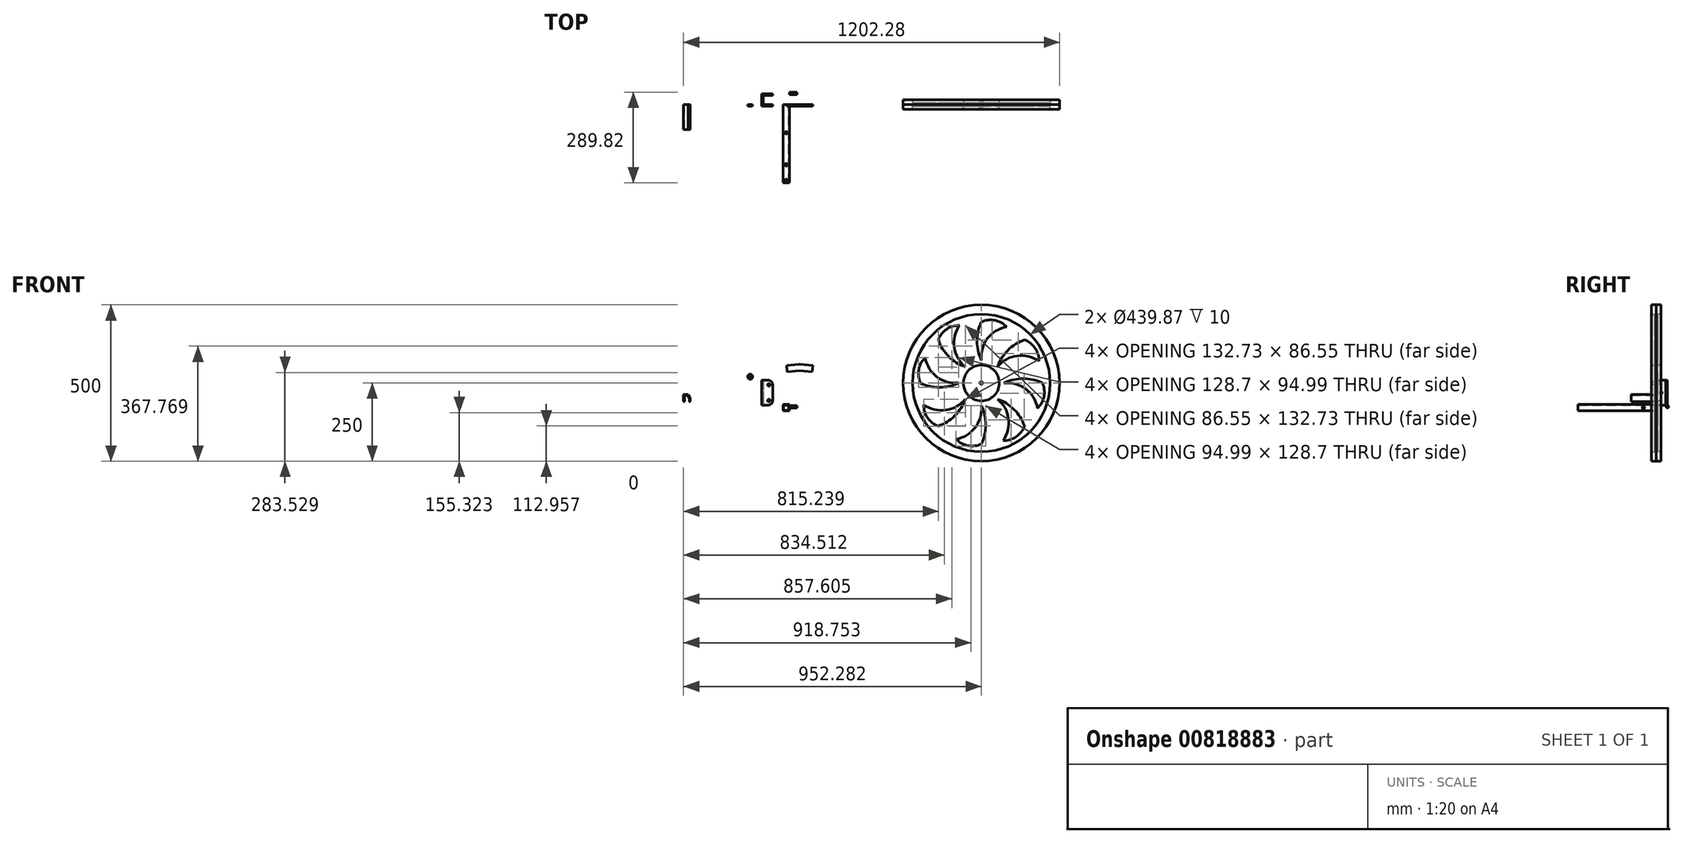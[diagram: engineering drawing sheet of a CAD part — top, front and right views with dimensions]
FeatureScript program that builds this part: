
annotation { "Feature Type Name" : "Feature", "Feature Type Description" : "" }
export const myFeature = defineFeature(function(context is Context, id is Id, definition is map)
    precondition{}
    {
        {
            var Q0;
            Q0=qCreatedBy(makeId("Front.planeOp"),FACE);
            var sketch = newSketch(context, id + "F0", { "sketchPlane" : qUnion([Q0])});
            skLineSegment(sketch, "E0.bottom", {"start": v(15, 40) * mm, "end": v(-15, 40) * mm});
            skLineSegment(sketch, "E0.top", {"start": v(15, -40) * mm, "end": v(-15, -40) * mm});
            skLineSegment(sketch, "E0.left", {"start": v(15, 40) * mm, "end": v(15, -40) * mm});
            skLineSegment(sketch, "E0.right", {"start": v(-15, 40) * mm, "end": v(-15, -40) * mm});
            skPoint(sketch, "E0.middle", {"position": v(0, 0) * mm});
            skLineSegment(sketch, "E1.bottom", {"start": v(-15, -40) * mm, "end": v(-20, -40) * mm});
            skLineSegment(sketch, "E1.top", {"start": v(-15, 40) * mm, "end": v(-20, 40) * mm});
            skLineSegment(sketch, "E1.left", {"start": v(-15, -40) * mm, "end": v(-15, 40) * mm});
            skLineSegment(sketch, "E1.right", {"start": v(-20, -40) * mm, "end": v(-20, 40) * mm});
            skCircle(sketch, "E2", {"center": v(3, 25) * mm, "radius": 4 * mm});
            skLineSegment(sketch, "E3", {"start": v(-15, 0) * mm, "end": v(9.6, 0) * mm, "construction": true});
            skCircle(sketch, "E4.MirrorC", {"center": v(3, -25) * mm, "radius": 4 * mm});
            skLineSegment(sketch, "E5.bottom", {"start": v(68.16, -57.9) * mm, "end": v(48.16, -57.9) * mm});
            skLineSegment(sketch, "E5.top", {"start": v(68.16, -37.9) * mm, "end": v(48.16, -37.9) * mm});
            skLineSegment(sketch, "E5.left", {"start": v(68.16, -57.9) * mm, "end": v(68.16, -37.9) * mm});
            skLineSegment(sketch, "E5.right", {"start": v(48.16, -57.9) * mm, "end": v(48.16, -37.9) * mm});
            skLineSegment(sketch, "E6.0", {"start": v(66.66, -56.4) * mm, "end": v(49.66, -56.4) * mm});
            skLineSegment(sketch, "E6.1", {"start": v(66.66, -56.4) * mm, "end": v(66.66, -39.4) * mm});
            skLineSegment(sketch, "E6.2", {"start": v(66.66, -39.4) * mm, "end": v(49.66, -39.4) * mm});
            skLineSegment(sketch, "E6.3", {"start": v(49.66, -56.4) * mm, "end": v(49.66, -39.4) * mm});
            skCircle(sketch, "E7", {"center": v(682.3, 30.98) * mm, "radius": 250 * mm});
            skCircle(sketch, "E8", {"center": v(682.3, 30.98) * mm, "radius": 57.27 * mm});
            skCircle(sketch, "E9", {"center": v(682.3, 30.98) * mm, "radius": 219.94 * mm});
            skCircle(sketch, "E10", {"center": v(682.3, 30.98) * mm, "radius": 4 * mm});
            skLineSegment(sketch, "E11", {"start": v(61.67, 67.05) * mm, "end": v(101.52, 70.54) * mm});
            skLineSegment(sketch, "E12", {"start": v(61.67, 67.05) * mm, "end": v(59.93, 86.98) * mm});
            skLineSegment(sketch, "E13", {"start": v(59.93, 86.98) * mm, "end": v(99.77, 90.46) * mm});
            skLineSegment(sketch, "E14", {"start": v(101.52, 70.54) * mm, "end": v(99.77, 90.46) * mm, "construction": true});
            skLineSegment(sketch, "E15", {"start": v(101.52, 70.54) * mm, "end": v(101.52, 109.2) * mm, "construction": true});
            skLineSegment(sketch, "E16.MirrorCS", {"start": v(101.52, 70.54) * mm, "end": v(103.26, 90.46) * mm, "construction": true});
            skLineSegment(sketch, "E17.MirrorCS", {"start": v(143.1, 86.98) * mm, "end": v(103.26, 90.46) * mm});
            skLineSegment(sketch, "E18.MirrorCS", {"start": v(141.36, 67.05) * mm, "end": v(143.1, 86.98) * mm});
            skLineSegment(sketch, "E19.MirrorCS", {"start": v(141.36, 67.05) * mm, "end": v(101.52, 70.54) * mm});
            skLineSegment(sketch, "E20", {"start": v(99.77, 90.46) * mm, "end": v(103.26, 90.46) * mm});
            skCircle(sketch, "E21", {"center": v(-56.88, 51) * mm, "radius": 8 * mm});
            skCircle(sketch, "E22", {"center": v(-56.88, 51) * mm, "radius": 4 * mm});
            skLineSegment(sketch, "E23.bottom", {"start": v(-266.99, -8.83) * mm, "end": v(-256.99, -8.83) * mm});
            skLineSegment(sketch, "E23.top", {"start": v(-266.99, -28.83) * mm, "end": v(-256.99, -28.83) * mm});
            skLineSegment(sketch, "E23.left", {"start": v(-266.99, -8.83) * mm, "end": v(-266.99, -28.83) * mm});
            skLineSegment(sketch, "E23.right", {"start": v(-256.99, -8.83) * mm, "end": v(-256.99, -28.83) * mm});
            skLineSegment(sketch, "E24", {"start": v(-256.99, -8.83) * mm, "end": v(-251.45, -18.83) * mm});
            skPoint(sketch, "E24.endSnap0", {"position": v(-256.99, -18.83) * mm});
            skLineSegment(sketch, "E25.0", {"start": v(-269.99, -5.83) * mm, "end": v(-269.99, -28.83) * mm});
            skLineSegment(sketch, "E25.1", {"start": v(-269.99, -5.83) * mm, "end": v(-255.22, -5.83) * mm});
            skLineSegment(sketch, "E25.2", {"start": v(-255.22, -5.83) * mm, "end": v(-248.83, -17.37) * mm});
            skLineSegment(sketch, "E26", {"start": v(-269.99, -28.83) * mm, "end": v(-266.99, -28.83) * mm});
            skLineSegment(sketch, "E27", {"start": v(-251.45, -18.83) * mm, "end": v(-251.45, -28.86) * mm});
            skLineSegment(sketch, "E28", {"start": v(-251.45, -28.86) * mm, "end": v(-248.83, -28.86) * mm});
            skLineSegment(sketch, "E29", {"start": v(-248.83, -28.86) * mm, "end": v(-248.83, -17.37) * mm});
            skArc(sketch, "E30", {"start": v(601.27, -148.4) * mm, "mid": v(662.98, -111.16) * mm, "end": v(682.3, -41.72) * mm});
            skArc(sketch, "E31", {"start": v(682.3, -164.11) * mm, "mid": v(696.26, -102.91) * mm, "end": v(682.3, -41.72) * mm});
            skArc(sketch, "E32", {"start": v(601.27, -148.4) * mm, "mid": v(639.28, -169.16) * mm, "end": v(682.3, -164.11) * mm});
            skArc(sketch, "E33.1.0", {"start": v(751.85, -153.16) * mm, "mid": v(769.15, -83.18) * mm, "end": v(733.7, -20.42) * mm});
            skArc(sketch, "E33.1.1", {"start": v(751.85, -153.16) * mm, "mid": v(793.4, -140.95) * mm, "end": v(820.24, -106.97) * mm});
            skArc(sketch, "E33.1.2", {"start": v(820.24, -106.97) * mm, "mid": v(786.84, -53.82) * mm, "end": v(733.7, -20.42) * mm});
            skArc(sketch, "E33.2.0", {"start": v(861.68, -50.04) * mm, "mid": v(824.43, 11.67) * mm, "end": v(754.99, 30.98) * mm});
            skArc(sketch, "E33.2.1", {"start": v(861.68, -50.04) * mm, "mid": v(882.43, -12.03) * mm, "end": v(877.38, 30.98) * mm});
            skArc(sketch, "E33.2.2", {"start": v(877.38, 30.98) * mm, "mid": v(816.18, 44.94) * mm, "end": v(754.99, 30.98) * mm});
            skArc(sketch, "E33.3.0", {"start": v(866.43, 100.53) * mm, "mid": v(796.45, 117.84) * mm, "end": v(733.7, 82.38) * mm});
            skArc(sketch, "E33.3.1", {"start": v(866.43, 100.53) * mm, "mid": v(854.22, 142.08) * mm, "end": v(820.24, 168.93) * mm});
            skArc(sketch, "E33.3.2", {"start": v(820.24, 168.93) * mm, "mid": v(767.1, 135.53) * mm, "end": v(733.7, 82.38) * mm});
            skArc(sketch, "E33.4.0", {"start": v(763.31, 210.37) * mm, "mid": v(701.6, 173.12) * mm, "end": v(682.3, 103.67) * mm});
            skArc(sketch, "E33.4.1", {"start": v(763.31, 210.37) * mm, "mid": v(725.3, 231.12) * mm, "end": v(682.3, 226.07) * mm});
            skArc(sketch, "E33.4.2", {"start": v(682.3, 226.07) * mm, "mid": v(668.33, 164.87) * mm, "end": v(682.3, 103.67) * mm});
            skArc(sketch, "E33.5.0", {"start": v(612.74, 215.12) * mm, "mid": v(595.43, 145.14) * mm, "end": v(630.89, 82.38) * mm});
            skArc(sketch, "E33.5.1", {"start": v(612.74, 215.12) * mm, "mid": v(571.19, 202.91) * mm, "end": v(544.34, 168.93) * mm});
            skArc(sketch, "E33.5.2", {"start": v(544.34, 168.93) * mm, "mid": v(577.74, 115.78) * mm, "end": v(630.89, 82.38) * mm});
            skArc(sketch, "E33.6.0", {"start": v(502.9, 112) * mm, "mid": v(540.15, 50.29) * mm, "end": v(609.6, 30.98) * mm});
            skArc(sketch, "E33.6.1", {"start": v(502.9, 112) * mm, "mid": v(482.15, 74) * mm, "end": v(487.2, 30.98) * mm});
            skArc(sketch, "E33.6.2", {"start": v(487.2, 30.98) * mm, "mid": v(548.4, 17.02) * mm, "end": v(609.6, 30.98) * mm});
            skArc(sketch, "E33.7.0", {"start": v(498.16, -38.57) * mm, "mid": v(568.13, -55.88) * mm, "end": v(630.89, -20.42) * mm});
            skArc(sketch, "E33.7.1", {"start": v(498.16, -38.57) * mm, "mid": v(510.36, -80.13) * mm, "end": v(544.34, -106.97) * mm});
            skArc(sketch, "E33.7.2", {"start": v(544.34, -106.97) * mm, "mid": v(597.49, -73.57) * mm, "end": v(630.89, -20.42) * mm});
            skSolve(sketch);
        }
        {
            var Q0;
            Q0=makeQuery(id+"F0.imprint","IMPRINT",FACE,{"disambiguationData":[TD([[makeQuery(id+"F0.imprint","IMPRINT",EDGE,{"derivedFrom":sQuery(id+"F0.wireOp",EDGE,"E1.bottom")}),-1.0]])]});
            var Q1;
            Q1=makeQuery(id+"F0.imprint","IMPRINT",FACE,{"disambiguationData":[TD([[makeQuery(id+"F0.imprint","IMPRINT",EDGE,{"derivedFrom":sQuery(id+"F0.wireOp",EDGE,"E0.bottom")}),1.0]])]});
            extrude(context, id + "F1", {"entities" : qUnion([Q0, Q1]), "depth" : 5 * mm, "offsetDistance" : 25 * mm});
        }
        {
            var Q0;
            Q0=makeQuery(id+"F0.imprint","IMPRINT",FACE,{"disambiguationData":[TD([[makeQuery(id+"F0.imprint","IMPRINT",EDGE,{"derivedFrom":sQuery(id+"F0.wireOp",EDGE,"E1.bottom")}),-1.0]])]});
            extrude(context, id + "F2", {"entities" : qUnion([Q0]), "operationType" : NewBodyOperationType.ADD, "oppositeDirection" : true, "depth" : 15 * mm, "offsetDistance" : 25 * mm});
        }
        {
            var Q0;
            Q0=makeQuery(id+"F1.opExtrude","SWEPT_BODY",BODY,{"disambiguationData":[OSD([sQuery(id+"F0.wireOp",EDGE,"E0.bottom"),sQuery(id+"F0.wireOp",EDGE,"E0.top"),sQuery(id+"F0.wireOp",EDGE,"E0.left"),sQuery(id+"F0.wireOp",EDGE,"E1.bottom"),sQuery(id+"F0.wireOp",EDGE,"E1.top"),sQuery(id+"F0.wireOp",EDGE,"E1.right"),sQuery(id+"F0.wireOp",EDGE,"E2"),sQuery(id+"F0.wireOp",EDGE,"E4.MirrorC")])]});
            var Q1;
            Q1=makeQuery(id+"F2.opExtrude","CAP_FACE",FACE,{"disambiguationData":[OSD([sQuery(id+"F0.wireOp",EDGE,"E1.bottom"),sQuery(id+"F0.wireOp",EDGE,"E1.top"),sQuery(id+"F0.wireOp",EDGE,"E1.left"),sQuery(id+"F0.wireOp",EDGE,"E1.right")])],"isStart":false});
            mirror(context, id + "F3", {"operationType" : NewBodyOperationType.ADD, "entities" : qUnion([Q0]), "mirrorPlane" : qUnion([Q1])});
        }
        {
            var Q0;
            {var subQ0=sQuery(id+"F0.wireOp",EDGE,"E1.right");var subQ1=makeQuery(id+"F2.boolean.opBoolean","MERGE",FACE,{"derivedFrom":[makeQuery(id+"F1.opExtrude","SWEPT_FACE",FACE,{"disambiguationData":[OSD([subQ0])]}),makeQuery(id+"F2.opExtrude","SWEPT_FACE",FACE,{"disambiguationData":[OSD([subQ0])]})]});Q0=makeQuery(id+"F3.boolean.opBoolean","MERGE",FACE,{"derivedFrom":[subQ1,makeQuery(id+"F3.opPattern","COPY",FACE,{"derivedFrom":subQ1,"instanceName":"1"})]});}
            var sketch = newSketch(context, id + "F4", { "sketchPlane" : qUnion([Q0])});
            skPoint(sketch, "E34", {"position": v(-15, 0) * mm});
            skPoint(sketch, "E34.positionSnap0", {"position": v(-15, -40) * mm});
            skSolve(sketch);
        }
        {
            var Q0;
            Q0=makeQuery(id+"F0.imprint","IMPRINT",FACE,{"disambiguationData":[TD([[makeQuery(id+"F0.imprint","IMPRINT",EDGE,{"derivedFrom":sQuery(id+"F0.wireOp",EDGE,"E5.bottom")}),-1.0]])]});
            extrude(context, id + "F5", {"entities" : qUnion([Q0]), "depth" : 250 * mm, "offsetDistance" : 25 * mm});
        }
        {
            var Q0;
            Q0=makeQuery(id+"F0.imprint","IMPRINT",FACE,{"disambiguationData":[TD([[makeQuery(id+"F0.imprint","IMPRINT",EDGE,{"derivedFrom":sQuery(id+"F0.wireOp",EDGE,"E7")}),1.0]])]});
            var Q1;
            Q1=makeQuery(id+"F0.imprint","IMPRINT",FACE,{"disambiguationData":[TD([[makeQuery(id+"F0.imprint","IMPRINT",EDGE,{"derivedFrom":sQuery(id+"F0.wireOp",EDGE,"E8")}),1.0]])]});
            var Q2;
            Q2 = qSketchRegion(id + "F4", true);
            extrude(context, id + "F6", {"entities" : qUnion([Q0, Q1, Q2]), "depth" : 15 * mm, "offsetDistance" : 25 * mm});
        }
        {
            var Q0;
            Q0=makeQuery(id+"F0.imprint","IMPRINT",FACE,{"disambiguationData":[TD([[makeQuery(id+"F0.imprint","IMPRINT",EDGE,{"derivedFrom":sQuery(id+"F0.wireOp",EDGE,"E8")}),-1.0]])]});
            extrude(context, id + "F7", {"entities" : qUnion([Q0]), "operationType" : NewBodyOperationType.ADD, "depth" : 5 * mm, "offsetDistance" : 25 * mm});
        }
        {
            var Q0;
            Q0=makeQuery(id+"F6.opExtrude","SWEPT_BODY",BODY,{"disambiguationData":[OSD([sQuery(id+"F0.wireOp",EDGE,"E7"),sQuery(id+"F0.wireOp",EDGE,"E9")])]});
            var Q1;
            {var subQ0=sQuery(id+"F0.wireOp",EDGE,"E9");var subQ1=sQuery(id+"F0.wireOp",EDGE,"E8");Q1=makeQuery(id+"F7.boolean.opBoolean","MERGE",FACE,{"derivedFrom":[makeQuery(id+"F6.opExtrude","CAP_FACE",FACE,{"disambiguationData":[OSD([sQuery(id+"F0.wireOp",EDGE,"E7"),subQ0])],"isStart":true}),makeQuery(id+"F6.opExtrude","CAP_FACE",FACE,{"disambiguationData":[OSD([subQ1,sQuery(id+"F0.wireOp",EDGE,"E10")])],"isStart":true}),makeQuery(id+"F7.opExtrude","CAP_FACE",FACE,{"disambiguationData":[OSD([subQ1,subQ0])],"isStart":true})]});}
            mirror(context, id + "F8", {"operationType" : NewBodyOperationType.ADD, "entities" : qUnion([Q0]), "mirrorPlane" : qUnion([Q1])});
        }
        {
            var Q0;
            Q0=makeQuery(id+"F1.opExtrude","SWEPT_EDGE",EDGE,{"disambiguationData":[OSD([sQuery(id+"F0.wireOp",EDGE,"E0.bottom"),sQuery(id+"F0.wireOp",EDGE,"E0.left")])]});
            var Q1;
            Q1=makeQuery(id+"F3.opPattern","COPY",EDGE,{"derivedFrom":makeQuery(id+"F1.opExtrude","SWEPT_EDGE",EDGE,{"disambiguationData":[OSD([sQuery(id+"F0.wireOp",EDGE,"E0.bottom"),sQuery(id+"F0.wireOp",EDGE,"E0.left")])]}),"instanceName":"1"});
            var Q2;
            Q2=makeQuery(id+"F3.opPattern","COPY",EDGE,{"derivedFrom":makeQuery(id+"F1.opExtrude","SWEPT_EDGE",EDGE,{"disambiguationData":[OSD([sQuery(id+"F0.wireOp",EDGE,"E0.top"),sQuery(id+"F0.wireOp",EDGE,"E0.left")])]}),"instanceName":"1"});
            var Q3;
            Q3=makeQuery(id+"F1.opExtrude","SWEPT_EDGE",EDGE,{"disambiguationData":[OSD([sQuery(id+"F0.wireOp",EDGE,"E0.top"),sQuery(id+"F0.wireOp",EDGE,"E0.left")])]});
            var Q4;
            {var subQ0=makeQuery(id+"F6.opExtrude","SWEPT_FACE",FACE,{"disambiguationData":[OSD([sQuery(id+"F0.wireOp",EDGE,"E7")])]});Q4=makeQuery(id+"F8.boolean.opBoolean","MERGE",FACE,{"derivedFrom":[subQ0,makeQuery(id+"F8.opPattern","COPY",FACE,{"derivedFrom":subQ0,"instanceName":"1"})]});}
            fillet(context, id + "F9", {"entities" : qUnion([Q0, Q1, Q2, Q3, Q4]), "radius" : 15 * mm, "tangentPropagation" : true, "allowEdgeOverflow" : false});
        }
        {
            var Q0;
            Q0=makeQuery(id+"F5.opExtrude","SWEPT_FACE",FACE,{"disambiguationData":[OSD([sQuery(id+"F0.wireOp",EDGE,"E5.top")])]});
            var sketch = newSketch(context, id + "F10", { "sketchPlane" : qUnion([Q0])});
            skPoint(sketch, "E35", {"position": v(58.16, -242) * mm});
            skPoint(sketch, "E35.positionSnap0", {"position": v(58.16, -250) * mm});
            skPoint(sketch, "E36", {"position": v(58.16, -192) * mm});
            skPoint(sketch, "E37", {"position": v(58.16, -90) * mm});
            skSolve(sketch);
        }
        {
            var Q0;
            Q0=makeQuery(id+"F0.imprint","IMPRINT",FACE,{"disambiguationData":[TD([[makeQuery(id+"F0.imprint","IMPRINT",EDGE,{"derivedFrom":sQuery(id+"F0.wireOp",EDGE,"E11")}),1.0]])]});
            var Q1;
            Q1=makeQuery(id+"F0.imprint","IMPRINT",FACE,{"disambiguationData":[TD([[makeQuery(id+"F0.imprint","IMPRINT",EDGE,{"derivedFrom":sQuery(id+"F0.wireOp",EDGE,"E21")}),1.0]])]});
            extrude(context, id + "F11", {"entities" : qUnion([Q0, Q1]), "depth" : 5 * mm, "offsetDistance" : 25 * mm});
        }
        {
            var Q0;
            Q0=makeQuery(id+"F0.imprint","IMPRINT",FACE,{"disambiguationData":[TD([[makeQuery(id+"F0.imprint","IMPRINT",EDGE,{"derivedFrom":sQuery(id+"F0.wireOp",EDGE,"E23.bottom")}),1.0]])]});
            extrude(context, id + "F12", {"entities" : qUnion([Q0]), "depth" : 80 * mm, "offsetDistance" : 25 * mm});
        }
        {
            var Q0;
            Q0=makeQuery(id+"F12.opExtrude","SWEPT_EDGE",EDGE,{"disambiguationData":[OSD([sQuery(id+"F0.wireOp",EDGE,"E27"),sQuery(id+"F0.wireOp",EDGE,"E28")])]});
            var Q1;
            Q1=makeQuery(id+"F12.opExtrude","SWEPT_EDGE",EDGE,{"disambiguationData":[OSD([sQuery(id+"F0.wireOp",EDGE,"E28"),sQuery(id+"F0.wireOp",EDGE,"E29")])]});
            var Q2;
            Q2=makeQuery(id+"F12.opExtrude","SWEPT_EDGE",EDGE,{"disambiguationData":[OSD([sQuery(id+"F0.wireOp",EDGE,"E25.2"),sQuery(id+"F0.wireOp",EDGE,"E29")])]});
            var Q3;
            Q3=makeQuery(id+"F12.opExtrude","SWEPT_EDGE",EDGE,{"disambiguationData":[OSD([sQuery(id+"F0.wireOp",EDGE,"E24"),sQuery(id+"F0.wireOp",EDGE,"E27")])]});
            var Q4;
            Q4=makeQuery(id+"F12.opExtrude","SWEPT_EDGE",EDGE,{"disambiguationData":[OSD([sQuery(id+"F0.wireOp",EDGE,"E23.bottom"),sQuery(id+"F0.wireOp",EDGE,"E23.right"),sQuery(id+"F0.wireOp",EDGE,"E24")])]});
            fillet(context, id + "F13", {"entities" : qUnion([Q0, Q1, Q2, Q3, Q4]), "radius" : 1.5 * mm, "tangentPropagation" : true, "allowEdgeOverflow" : false});
        }
        {
            var Q0;
            Q0=makeQuery(id+"F5.opExtrude","SWEPT_FACE",FACE,{"disambiguationData":[OSD([sQuery(id+"F0.wireOp",EDGE,"E5.left")])]});
            var sketch = newSketch(context, id + "F14", { "sketchPlane" : qUnion([Q0])});
            skPoint(sketch, "E38", {"position": v(-41.18, -47.9) * mm});
            skPoint(sketch, "E38.positionSnap0", {"position": v(0, -47.9) * mm});
            skCircle(sketch, "E39", {"center": v(-41.18, -47.9) * mm, "radius": 4 * mm});
            skCircle(sketch, "E40", {"center": v(35.82, -44.75) * mm, "radius": 4 * mm});
            skSolve(sketch);
        }
        {
            var Q0;
            Q0=sQuery(id+"F4.wireOp",VERTEX,"E34");
            var Q1;
            Q1=sQuery(id+"F10.wireOp",VERTEX,"E35");
            var Q2;
            Q2=sQuery(id+"F10.wireOp",VERTEX,"E36");
            var Q3;
            Q3=sQuery(id+"F10.wireOp",VERTEX,"E37");
            var Q4;
            Q4=sQuery(id+"F14.wireOp",VERTEX,"E38");
            var Q5;
            Q5=makeQuery(id+"F1.opExtrude","SWEPT_BODY",BODY,{"disambiguationData":[OSD([sQuery(id+"F0.wireOp",EDGE,"E0.bottom"),sQuery(id+"F0.wireOp",EDGE,"E0.top"),sQuery(id+"F0.wireOp",EDGE,"E0.left"),sQuery(id+"F0.wireOp",EDGE,"E1.bottom"),sQuery(id+"F0.wireOp",EDGE,"E1.top"),sQuery(id+"F0.wireOp",EDGE,"E1.right"),sQuery(id+"F0.wireOp",EDGE,"E2"),sQuery(id+"F0.wireOp",EDGE,"E4.MirrorC")])]});
            var Q6;
            Q6=makeQuery(id+"F5.opExtrude","SWEPT_BODY",BODY,{"disambiguationData":[OSD([sQuery(id+"F0.wireOp",EDGE,"E5.bottom"),sQuery(id+"F0.wireOp",EDGE,"E5.top"),sQuery(id+"F0.wireOp",EDGE,"E5.left"),sQuery(id+"F0.wireOp",EDGE,"E5.right"),sQuery(id+"F0.wireOp",EDGE,"E6.0"),sQuery(id+"F0.wireOp",EDGE,"E6.1"),sQuery(id+"F0.wireOp",EDGE,"E6.2"),sQuery(id+"F0.wireOp",EDGE,"E6.3")])]});
            hole(context, id + "F15", {"style" : HoleStyle.SIMPLE, "endStyle" : HoleEndStyle.THROUGH, "holeDiameter" : 8 * mm, "majorDiameter" : 5 * mm, "isTappedThrough" : true, "tappedDepth" : 12 * mm, "tapClearance" : 3, "startFromSketch" : true, "locations" : qUnion([Q0, Q1, Q2, Q3, Q4]), "scope" : qUnion([Q5, Q6])});
        }
        {
            var Q0;
            Q0=makeQuery(id+"F14.imprint","IMPRINT",FACE,{"disambiguationData":[TD([[makeQuery(id+"F14.imprint","IMPRINT",EDGE,{"derivedFrom":sQuery(id+"F14.wireOp",EDGE,"E40")}),1.0]])]});
            extrude(context, id + "F16", {"entities" : qUnion([Q0]), "depth" : 25 * mm, "offsetDistance" : 25 * mm});
        }
    });
